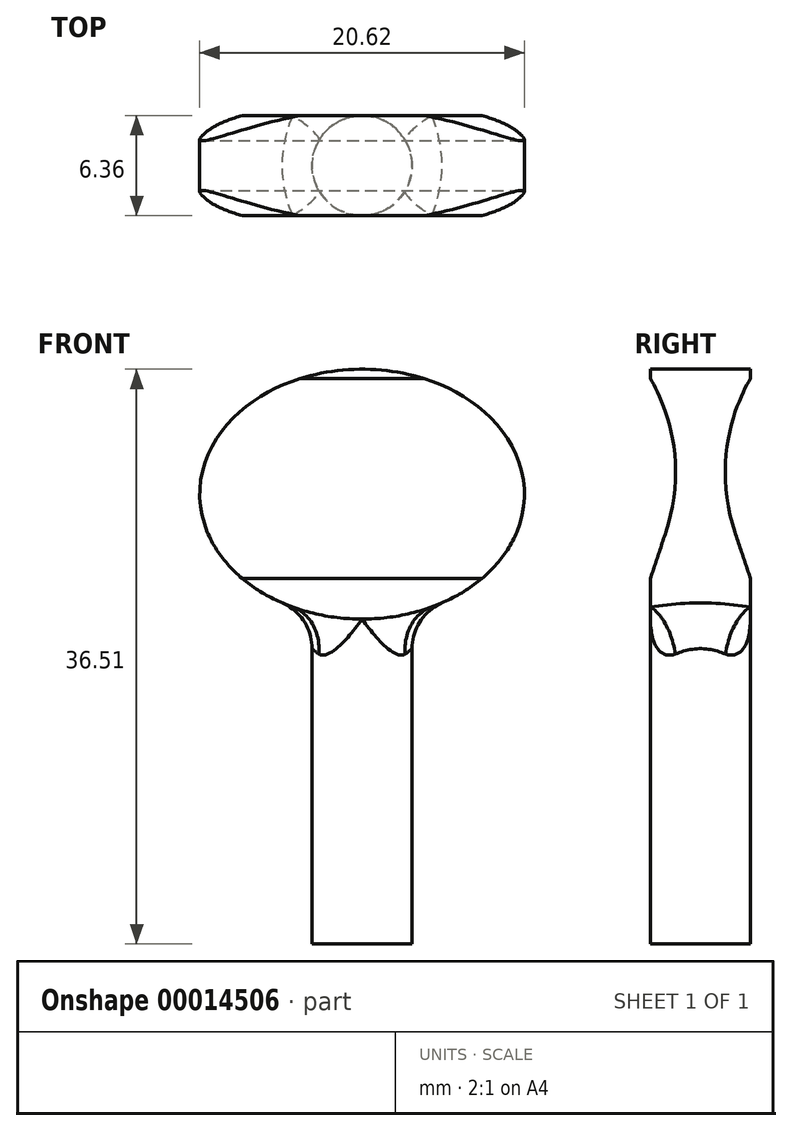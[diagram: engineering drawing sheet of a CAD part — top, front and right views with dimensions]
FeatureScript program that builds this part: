
annotation { "Feature Type Name" : "Feature", "Feature Type Description" : "" }
export const myFeature = defineFeature(function(context is Context, id is Id, definition is map)
    precondition{}
    {
        {
            var Q0;
            Q0=qCreatedBy(makeId("Top.planeOp"),FACE);
            var sketch = newSketch(context, id + "F0", { "sketchPlane" : qUnion([Q0])});
            skCircle(sketch, "E0", {"center": v(0, 0) * mm, "radius": 3.18 * mm});
            skSolve(sketch);
        }
        {
            var Q0;
            Q0=qCreatedBy(makeId("Right.planeOp"),FACE);
            var sketch = newSketch(context, id + "F1", { "sketchPlane" : qUnion([Q0])});
            skLineSegment(sketch, "E1", {"start": v(0, -63.5) * mm, "end": v(0, 63.5) * mm});
            skSolve(sketch);
        }
        {
            var Q0;
            Q0 = qSketchRegion(id + "F0", true);
            extrude(context, id + "F2", {"entities" : qUnion([Q0]), "depth" : 25.4 * mm});
        }
        {
            var Q0;
            Q0=qCreatedBy(makeId("Front.planeOp"),FACE);
            var sketch = newSketch(context, id + "F3", { "sketchPlane" : qUnion([Q0])});
            skEllipse(sketch, "E2", {"center": v(0, 28.58) * mm, "majorRadius": 10.31 * mm, "minorRadius": 7.94 * mm, "majorAxis": v(1, 0)});
            skSolve(sketch);
        }
        {
            var Q0;
            Q0=makeQuery(id+"F3.imprint","IMPRINT",FACE,{"disambiguationData":[TD([[makeQuery(id+"F3.imprint","IMPRINT",EDGE,{"derivedFrom":sQuery(id+"F3.wireOp",EDGE,"E2")}),1.0]])]});
            extrude(context, id + "F4", {"entities" : qUnion([Q0]), "operationType" : NewBodyOperationType.ADD, "depth" : 6.35 * mm, "symmetric" : true});
        }
        {
            var Q0;
            Q0=makeQuery(id+"F4.boolean.opBoolean","INTERSECT",EDGE,{"disambiguationData":[OD(1.0)],"derivedFrom":[makeQuery(id+"F2.opExtrude","SWEPT_FACE",FACE,{"disambiguationData":[OSD([sQuery(id+"F0.wireOp",EDGE,"E0")])]}),makeQuery(id+"F4.opExtrude","SWEPT_FACE",FACE,{"disambiguationData":[OSD([sQuery(id+"F3.wireOp",EDGE,"E2")])]})]});
            fillet(context, id + "F5", {"entities" : qUnion([Q0]), "radius" : 3.17 * mm, "tangentPropagation" : true, "allowEdgeOverflow" : false});
        }
        {
            var Q0;
            Q0=qCreatedBy(makeId("Right.planeOp"),FACE);
            var sketch = newSketch(context, id + "F6", { "sketchPlane" : qUnion([Q0])});
            skArc(sketch, "E3", {"start": v(6.02, 39.23) * mm, "mid": v(2.06, 33.3) * mm, "end": v(2.19, 26.18) * mm});
            skLineSegment(sketch, "E4", {"start": v(2.19, 26.18) * mm, "end": v(5.25, 17) * mm});
            skLineSegment(sketch, "E5", {"start": v(5.25, 17) * mm, "end": v(10.18, 17) * mm});
            skLineSegment(sketch, "E6", {"start": v(6.02, 39.23) * mm, "end": v(6.02, 17) * mm});
            skArc(sketch, "E7.MirrorCS", {"start": v(-6.02, 39.23) * mm, "mid": v(-2.06, 33.3) * mm, "end": v(-2.19, 26.18) * mm});
            skLineSegment(sketch, "E8.MirrorCS", {"start": v(-2.19, 26.18) * mm, "end": v(-5.25, 17) * mm});
            skLineSegment(sketch, "E9.MirrorCS", {"start": v(-6.02, 39.23) * mm, "end": v(-6.02, 17) * mm});
            skLineSegment(sketch, "E10.MirrorCS", {"start": v(-5.25, 17) * mm, "end": v(-10.18, 17) * mm});
            skSolve(sketch);
        }
        {
            var Q0;
            Q0 = qSketchRegion(id + "F6", true);
            extrude(context, id + "F7", {"entities" : qUnion([Q0]), "operationType" : NewBodyOperationType.REMOVE, "oppositeDirection" : true, "depth" : 50.8 * mm, "symmetric" : true});
        }
    });
